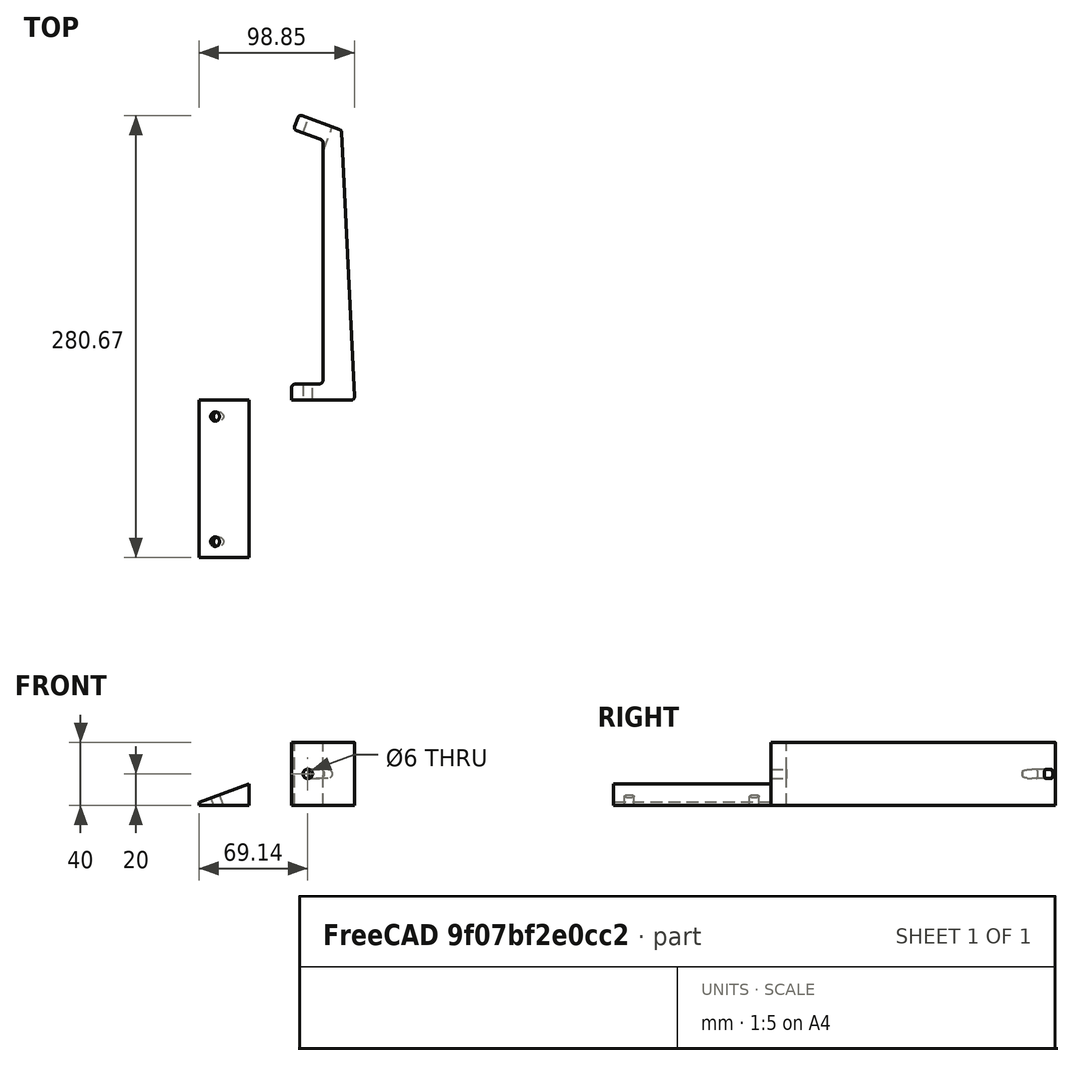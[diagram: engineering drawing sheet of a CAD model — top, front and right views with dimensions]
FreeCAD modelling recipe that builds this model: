
FCSTD DOCUMENT  (FreeCAD 0.19R)
Label: SolarProp20deg
License: All rights reserved
LicenseURL: http://en.wikipedia.org/wiki/All_rights_reserved
objects: Sketcher::SketchObject×5, PartDesign::Fillet×4, PartDesign::Pocket×3, PartDesign::Pad×2, PartDesign::Body×2, Mesh::Feature×1
note: 25 computed .brp shape members not serialized (recipe doc carries the construction recipe); baked Part::Feature solids carry a one-line shape summary decoded from their .brp

FEATURE [Sketcher::SketchObject] Sketch
  FullyConstrained = true
  MapMode = 5
  Support = -> [XY_Plane]
  sketch-geometry (10):
    g0: LineSegment StartX=530 StartY=0 StartZ=0 EndX=0 EndY=0 EndZ=0
    g1: LineSegment StartX=31.9629 StartY=181.271 StartZ=0 EndX=530 EndY=0 EndZ=0
    g2: LineSegment StartX=27 StartY=0 StartZ=0 EndX=27 EndY=10 EndZ=0
    g3: LineSegment StartX=27 StartY=10 StartZ=0 EndX=47 EndY=10 EndZ=0
    g4: LineSegment StartX=47 StartY=10 StartZ=0 EndX=47 EndY=165 EndZ=0
    g5: LineSegment StartX=47 StartY=165 StartZ=0 EndX=28.2061 EndY=171.84 EndZ=0
    g6: LineSegment StartX=28.2061 StartY=171.84 StartZ=0 EndX=31.6263 EndY=181.237 EndZ=0
    g7: LineSegment StartX=31.6263 StartY=181.237 StartZ=0 EndX=58.7052 EndY=171.381 EndZ=0
    g8: LineSegment StartX=58.7052 StartY=171.381 StartZ=0 EndX=67 EndY=0 EndZ=0
    g9: LineSegment StartX=67 StartY=0 StartZ=0 EndX=27 EndY=0 EndZ=0
  constraints (30):
    c: PointOnObject(g0,g-1)
    c: Coincident(g0,g-1)
    c: Distance(g0) = 530
    c: Coincident(g1,g0)
    c: Angle(g1) = -0.349066
    c: Distance(g1) = 530
    c: PointOnObject(g2,g0)
    c: Coincident(g2,g3)
    c: Coincident(g3,g4)
    c: Vertical(g4)
    c: Coincident(g4,g5)
    c: Coincident(g5,g6)
    c: Coincident(g6,g7)
    c: Coincident(g7,g8)
    c: PointOnObject(g8,g0)
    c: Coincident(g8,g9)
    c: Coincident(g9,g2)
    c: Horizontal(g3)
    c: Distance(g2) = 10
    c: Distance(g9) = 40
    c: Vertical(g2)
    c: DistanceX(g3) = 47
    c: Angle(g5) = 2.79253
    c: Parallel(g7,g5)
    c: Perpendicular(g5,g6)
    c: Distance(g6) = 10
    c: Distance(g4,g8) = 12
    c: Distance(g5) = 20
    c: Distance(g3) = 20
    c: Distance(g4) = 155
FEATURE [PartDesign::Pad] Pad
  Direction = (1,1,1)
  Length = 40
  Length2 = 100
  Profile = -> Sketch
  Type = 0
FEATURE [PartDesign::Fillet] Fillet
  Base = -> Pad [Edge5]
  BaseFeature = -> Pad
  Radius = 3
  SupportTransform = false
FEATURE [PartDesign::Fillet] Fillet001
  Base = -> Fillet [Edge23]
  BaseFeature = -> Fillet
  Radius = 3
  SupportTransform = false
FEATURE [PartDesign::Fillet] Fillet002
  Base = -> Fillet001 [Edge18,Edge20]
  BaseFeature = -> Fillet001
  Radius = 2
  SupportTransform = false
FEATURE [PartDesign::Fillet] Fillet003
  Base = -> Fillet002 [Edge28,Edge24,Edge20]
  BaseFeature = -> Fillet002
  Radius = 2
  SupportTransform = false
FEATURE [Sketcher::SketchObject] Sketch001
  FullyConstrained = true
  MapMode = 5
  Placement = pos=(0,10,0) rot=(0,0.707107,0.707107;3.14159rad)
  Support = -> [Fillet003]
  sketch-geometry (1):
    g0: Circle CenterX=-37.19 CenterY=20 CenterZ=0 NormalX=0 NormalY=0 NormalZ=1 AngleXU=0 Radius=3
  constraints (3):
    c: Diameter(g0) = 6
    c: DistanceY(g0) = 20
    c: DistanceX(g0) = -37.19
FEATURE [PartDesign::Pocket] Pocket
  BaseFeature = -> Fillet003
  Length = 5
  Length2 = 100
  Profile = -> Sketch001
  Type = 1
FEATURE [Sketcher::SketchObject] Sketch002
  FullyConstrained = false
  MapMode = 5
  Placement = pos=(61.9481,170.201,0) rot=(0.123724,0.701674,0.701674;2.8954rad)
  Support = -> [Pocket]
  sketch-geometry (4):
    g0: ArcOfCircle CenterX=12.7754 CenterY=20 CenterZ=0 NormalX=0 NormalY=0 NormalZ=1 AngleXU=0 Radius=3 StartAngle=1.5708 EndAngle=4.71239
    g1: ArcOfCircle CenterX=22.7754 CenterY=20 CenterZ=0 NormalX=0 NormalY=0 NormalZ=1 AngleXU=0 Radius=3 StartAngle=4.71239 EndAngle=7.85398
    g2: LineSegment StartX=12.7754 StartY=17 StartZ=0 EndX=22.7754 EndY=17 EndZ=0
    g3: LineSegment StartX=12.7754 StartY=23 StartZ=0 EndX=22.7754 EndY=23 EndZ=0
  constraints (9):
    c: Tangent(g0,g3) = 1.5708
    c: Tangent(g0,g2) = -1.5708
    c: Tangent(g2,g1) = -1.5708
    c: Tangent(g3,g1) = 1.5708
    c: Horizontal(g2)
    c: Equal(g0,g1)
    c: Distance(g1,g1) = 6
    c: DistanceY(g1) = 20
    c: Distance(g0,g1) = 10
FEATURE [PartDesign::Pocket] Pocket001
  BaseFeature = -> Pocket
  Length = 15
  Length2 = 100
  Profile = -> Sketch002
  Type = 0
FEATURE [PartDesign::Body] Body
  Group = -> [Sketch,Pad,Fillet,Fillet001,Fillet002,Fillet003,Sketch001,Pocket,Sketch002,Pocket001]
  Origin = -> Origin
  Tip = -> Pocket001
FEATURE [Mesh::Feature] Mesh  label="Pocket001 (Meshed)"
FEATURE [Sketcher::SketchObject] Sketch003
  FullyConstrained = true
  MapMode = 5
  Placement = pos=(0,0,0) rot=(1,0,0;1.5708rad)
  Support = -> [XZ_Plane001]
  sketch-geometry (4):
    g0: LineSegment StartX=0 StartY=0 StartZ=0 EndX=-31.9495 EndY=0 EndZ=0
    g1: LineSegment StartX=-31.9495 StartY=0 StartZ=0 EndX=-31.9495 EndY=2 EndZ=0
    g2: LineSegment StartX=-31.9495 StartY=2 StartZ=0 EndX=0 EndY=13.6287 EndZ=0
    g3: LineSegment StartX=0 StartY=13.6287 StartZ=0 EndX=0 EndY=0 EndZ=0
  constraints (11):
    c: Coincident(g-1,g0)
    c: PointOnObject(g0,g-1)
    c: Coincident(g0,g1)
    c: Coincident(g1,g2)
    c: PointOnObject(g2,g-2)
    c: Coincident(g2,g3)
    c: Coincident(g3,g0)
    c: Angle(g2) = 0.349066
    c: Distance(g1) = 2
    c: Vertical(g1)
    c: Distance(g2) = 34
FEATURE [PartDesign::Pad] Pad001
  Direction = (1,1,1)
  Length = 100
  Length2 = 100
  Placement = pos=(0,0,0) rot=(1,0,0;1.5708rad)
  Profile = -> Sketch003
  Type = 0
FEATURE [Sketcher::SketchObject] Sketch004
  ExternalGeometry = -> [Pad001]
  FullyConstrained = true
  MapMode = 5
  Placement = pos=(-4.38017,8e-15,12.0344) rot=(-0.173648,0,0.984808;3.14159rad)
  Support = -> [Pad001]
  sketch-geometry (2):
    g0: Circle CenterX=18.3387 CenterY=90 CenterZ=0 NormalX=0 NormalY=0 NormalZ=1 AngleXU=0 Radius=3
    g1: Circle CenterX=18.3387 CenterY=10.5 CenterZ=0 NormalX=0 NormalY=0 NormalZ=1 AngleXU=0 Radius=3
  constraints (6):
    c: DistanceY(g1) = 10.5
    c: Distance(g1,g0) = 79.5
    c: Diameter(g0) = 6
    c: Equal(g0,g1)
    c: DistanceX(g1,g0) = 0
    c: Distance(g0,g-3) = 11
FEATURE [PartDesign::Pocket] Pocket002
  BaseFeature = -> Pad001
  Length = 5
  Length2 = 100
  Placement = pos=(0,0,0) rot=(1,0,0;1.5708rad)
  Profile = -> Sketch004
  Type = 1
FEATURE [PartDesign::Body] Body001
  Group = -> [Sketch003,Pad001,Sketch004,Pocket002]
  Origin = -> Origin001
  Tip = -> Pocket002
